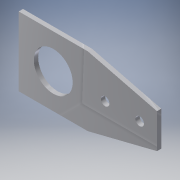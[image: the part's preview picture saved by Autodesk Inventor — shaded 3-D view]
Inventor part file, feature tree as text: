
AUTODESK INVENTOR PART (.ipt)
format: ipt  version: 2016 (Build 200138000, 138)  size: 113,664 bytes
history: native  units: in
note: dims shown in document units (in); Inventor stores cm internally (conversion verified against a paired STEP export)
features: extrude x1, sketch x1
ambient origin geometry x8: Origin, YZ Plane, XZ Plane, XY Plane, X Axis, Y Axis, Z Axis, Center Point
bodies: Solid1 (feature_tree)
feature tree (2):
  extrude  "Extrusion1"  Depth=2.0in
  sketch  "Sketch1"  dims[d1=2.0in d2=2.0in d3=2.0in d4=1.0in d5=1.125in d6=1.0in d7=1.0in d8=0.25in d9=0.25in d10=0.5in d11=1.0in d12=0.125in d13=0.0in]
